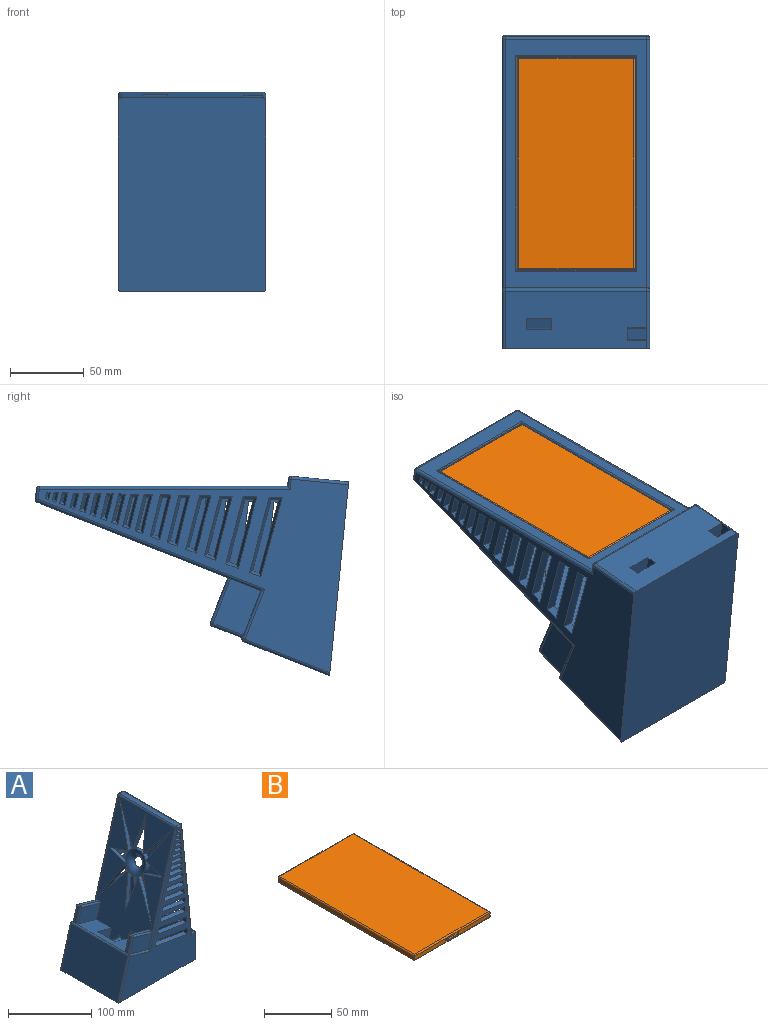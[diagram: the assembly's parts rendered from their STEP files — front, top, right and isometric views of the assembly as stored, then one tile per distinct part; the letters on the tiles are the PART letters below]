
ASSEMBLY  parts=2 mates=1
PART A: 294 faces, bbox 131.9x100x210.6 mm
  f0: plane 201.07x93mm, normal (0.96,0,-0.27), area 15915.5mm2, adj f3,f4,f9,f10,f11,f26,f27,f28
  f1: plane 200.88x96mm, normal (-0.96,0,0.27), area 12476.6mm2, adj f11,f18,f24,f25,f27,f28,f30,f31
  f2: plane 208x127.8mm, normal (0,1,0), area 9393.5mm2, adj f19,f23,f73,f78,f84,f86,f89,f94
  f3: plane 201.07x77.33mm, normal (0,-1,0), area 6368.6mm2, adj f0,f4,f26,f224,f225,f226,f227,f228
  f4: plane 201.07x93mm, normal (-1,0,-0.1), area 7026.5mm2, adj f0,f3,f6,f7,f26,f55,f136,f137
  f5: plane 96x38.96mm, normal (1,0,0), area 3497.2mm2, adj f19,f90,f92,f94,f152,f153,f154,f155
  f6: plane 80x4.04mm, normal (0.1,0,-1), area 291.7mm2, adj f4,f136,f137,f141,f142,f143,f149,f150
  f7: plane 80x4.04mm, normal (-0.1,0,1), area 292mm2, adj f4,f136,f137,f138,f139,f140,f148,f151
  f8: plane 167.24x96mm, normal (1,0,0.1), area 4160.7mm2, adj f21,f71,f73,f74,f144,f147,f292,f293
  f9: plane 6.2x1.71mm, normal (0.02,0,-1), area 5.3mm2, adj f0,f11,f134
  f10: plane 6.2x1.71mm, normal (0.02,0,-1), area 5.3mm2, adj f0,f95,f135
  f11: plane 24.74x13.23mm, normal (0,-1,0), area 152mm2, adj f0,f1,f9,f97
  f12: plane 5x1.82mm, normal (0.42,-0.91,0), area 5mm2, adj f17,f124,f131,f132,f133
  f13: plane 5x1.98mm, normal (0.99,-0.13,0), area 5mm2, adj f17,f122,f128,f129,f130
  f14: plane 5x1.98mm, normal (-0.99,0.13,0), area 5mm2, adj f17,f122,f128,f129,f130
  f15: plane 5x1.43mm, normal (-0.71,-0.7,0), area 5mm2, adj f17,f121,f125,f126,f127
  f16: plane 5x1.43mm, normal (0.71,0.7,0), area 5mm2, adj f17,f121,f125,f126,f127
  f17: plane 100x32.21mm, normal (0,0,1), area 2726.6mm2, adj f12,f13,f14,f15,f16,f27,f28,f59
  f18: plane 96x33.08mm, normal (0.27,0,0.96), area 2022.9mm2, adj f1,f24,f25,f56,f82,f86,f87,f101
  f19: plane 131.88x100mm, normal (0,0,-1), area 13184.7mm2, adj f2,f5,f20,f54,f83,f89,f90,f94
  f20: plane 208x127.8mm, normal (0,-1,0), area 9393.5mm2, adj f19,f22,f71,f75,f80,f82,f83,f90
  f21: plane 96x5mm, normal (0,0,1), area 479.5mm2, adj f8,f22,f23,f92
  f22: cylinder r=2mm len=6.81mm, axis (-1,0,0), area 17.8mm2, adj f20,f21,f71,f91
  f23: cylinder r=2mm len=6.81mm, axis (1,0,0), area 17.8mm2, adj f2,f21,f73,f93
  f24: plane 51.2x36.71mm, normal (0,-1,0), area 1128.6mm2, adj f1,f18,f56,f57,f68,f69,f70
  f25: plane 51.2x36.71mm, normal (0,1,0), area 1128.6mm2, adj f1,f18,f56,f57,f65,f66,f67
  f26: plane 93x77.33mm, normal (0,0,1), area 4899.7mm2, adj f0,f3,f4,f27,f28,f55,f60,f61
  f27: plane 30.1x8.4mm, normal (0,1,0), area 170.7mm2, adj f0,f1,f17,f26,f57,f58,f59,f60
  f28: plane 30.1x8.4mm, normal (0,-1,0), area 170.7mm2, adj f0,f1,f17,f26,f57,f58,f59,f63
  f29: cylinder r=17.15mm len=7.66mm, axis (-0.96,0,0.27), area 52.7mm2, adj f0,f30,f31,f98
  f30: plane 49.59x36.3mm, normal (-0.16,0.81,-0.57), area 365.4mm2, adj f0,f1,f29,f31,f98
  f31: plane 55.63x30.11mm, normal (0.13,-0.88,0.45), area 377.4mm2, adj f0,f1,f29,f30,f98
  f32: cylinder r=17.15mm len=17.03mm, axis (-0.96,0,0.27), area 105.4mm2, adj f0,f33,f34,f98
  f33: plane 49.43x19.37mm, normal (0.05,-0.99,0.16), area 298.6mm2, adj f0,f1,f32,f34,f98
  f34: plane 49.56x19.41mm, normal (0.05,0.99,0.16), area 299.6mm2, adj f0,f1,f32,f33,f98
  f35: cylinder r=17.15mm len=7.57mm, axis (-0.96,0,0.27), area 52.7mm2, adj f0,f36,f37,f98
  f36: plane 55.41x30.24mm, normal (-0.13,-0.88,-0.46), area 376.5mm2, adj f0,f1,f35,f37,f98
  f37: plane 49.46x36.53mm, normal (0.16,0.81,0.57), area 365.5mm2, adj f0,f1,f35,f36,f98
  f38: cylinder r=17.15mm len=17.98mm, axis (-0.96,0,0.27), area 105.2mm2, adj f0,f39,f40,f98
  f39: plane 30.05x9.7mm, normal (-0.26,-0.27,-0.93), area 184.7mm2, adj f0,f1,f38,f40,f98
  f40: plane 30.18x9.92mm, normal (0.26,-0.27,0.92), area 185.8mm2, adj f0,f1,f38,f39,f98
  f41: cylinder r=17.15mm len=17.03mm, axis (-0.96,0,0.27), area 105.4mm2, adj f0,f42,f43,f98
  f42: plane 49.44x19.36mm, normal (-0.05,0.99,-0.16), area 298.6mm2, adj f0,f1,f41,f43,f98
  f43: plane 49.56x19.4mm, normal (-0.05,-0.99,-0.16), area 299.6mm2, adj f0,f1,f41,f42,f98
  f44: cylinder r=17.15mm len=7.57mm, axis (-0.96,0,0.27), area 52.7mm2, adj f0,f45,f46,f98
  f45: plane 55.42x30.24mm, normal (0.13,0.88,0.46), area 376.5mm2, adj f0,f1,f44,f46,f98
  f46: plane 49.47x36.53mm, normal (-0.16,-0.81,-0.57), area 365.5mm2, adj f0,f1,f44,f45,f98
  f47: cylinder r=17.15mm len=7.66mm, axis (-0.96,0,0.27), area 52.7mm2, adj f0,f48,f49,f98
  f48: plane 49.59x36.3mm, normal (0.16,-0.81,0.57), area 365.4mm2, adj f0,f1,f47,f49,f98
  f49: plane 55.63x30.11mm, normal (-0.13,0.88,-0.45), area 377.4mm2, adj f0,f1,f47,f48,f98
  f50: cylinder r=17.15mm len=17.98mm, axis (-0.96,0,0.27), area 105.2mm2, adj f0,f51,f52,f98
  f51: plane 30.05x9.62mm, normal (0.27,0.27,0.93), area 184.5mm2, adj f0,f1,f50,f52,f98
  f52: plane 30.18x10mm, normal (-0.26,0.28,-0.92), area 185.9mm2, adj f0,f1,f50,f51,f98
  f53: plane 96x6.98mm, normal (0,0,1), area 669.7mm2, adj f74,f75,f78,f79
  f54: plane 96x60.08mm, normal (-0.96,0,0.27), area 5998.6mm2, adj f19,f83,f87,f89
  f55: plane 201.07x77.33mm, normal (0,1,0), area 6683.8mm2, adj f0,f4,f26,f160,f161,f162,f163,f164
  f56: plane 44.32x30mm, normal (0.96,0,-0.27), area 1383mm2, adj f18,f24,f25,f57
  f57: plane 30x24.04mm, normal (0.27,0,0.96), area 416.4mm2, adj f1,f24,f25,f27,f28,f56,f58
  f58: plane 16x2.01mm, normal (0,0,-1), area 32.2mm2, adj f27,f28,f57,f59
  f59: plane 16x8.4mm, normal (1,0,0), area 134.4mm2, adj f17,f27,f28,f58
  f60: plane 7.85x0.39mm, normal (1,0,0), area 3.1mm2, adj f17,f26,f27,f61
  f61: plane 69.9x0.39mm, normal (0,1,0), area 27.4mm2, adj f17,f26,f60,f64
  f62: plane 69.9x0.39mm, normal (0,-1,0), area 27.4mm2, adj f17,f26,f63,f64
  f63: plane 8.36x0.39mm, normal (1,0,0), area 3.3mm2, adj f17,f26,f28,f62
  f64: plane 32.21x0.39mm, normal (-1,0,0), area 12.6mm2, adj f17,f26,f61,f62
  f65: cylinder r=0.5mm len=23.25mm, axis (-0.96,0,0.27), area 37.5mm2, adj f25,f66,f67
  f66: plane 0.96x0.5mm, normal (-0.96,0,0.27), area 0.4mm2, adj f25,f65
  f67: plane 0.96x0.5mm, normal (0.96,0,-0.27), area 0.4mm2, adj f25,f65
  f68: cylinder r=0.5mm len=23.25mm, axis (-0.96,0,0.27), area 37.5mm2, adj f24,f69,f70
  f69: plane 0.96x0.5mm, normal (-0.96,0,0.27), area 0.4mm2, adj f24,f68
  f70: plane 0.96x0.5mm, normal (0.96,0,-0.27), area 0.4mm2, adj f24,f68
  f71: cylinder r=2mm len=169.24mm, axis (-0.1,0,1), area 530mm2, adj f8,f20,f22,f72
  f72: sphere r=2mm, area 5.9mm2, adj f71,f74,f75
  f73: cylinder r=2mm len=169.24mm, axis (0.1,0,-1), area 530mm2, adj f2,f8,f23,f76
  f74: cylinder r=2mm len=96mm, axis (0,-1,0), area 282.7mm2, adj f8,f53,f72,f76
  f75: cylinder r=2mm len=6.98mm, axis (1,0,0), area 21.9mm2, adj f20,f53,f72,f77
  f76: sphere r=2mm, area 5.9mm2, adj f73,f74,f78
  f77: sphere r=2mm, area 5.2mm2, adj f75,f79,f80
  f78: cylinder r=2mm len=6.98mm, axis (-1,0,0), area 21.9mm2, adj f2,f53,f76,f81
  f79: cylinder r=2mm len=96mm, axis (0,-1,0), area 248.1mm2, adj f1,f53,f77,f81
  f80: cylinder r=2mm len=159.03mm, axis (-0.27,0,-0.96), area 513.8mm2, adj f1,f20,f77,f82,f103
  f81: sphere r=2mm, area 5.2mm2, adj f78,f79,f84
  f82: cylinder r=2mm len=35.55mm, axis (-0.96,0,0.27), area 110.4mm2, adj f18,f20,f80,f85,f103
  f83: cylinder r=2mm len=60.63mm, axis (-0.27,0,-0.96), area 195.7mm2, adj f19,f20,f54,f85
  f84: cylinder r=2mm len=159.03mm, axis (0.27,0,0.96), area 513.8mm2, adj f1,f2,f81,f86,f100
  f85: sphere r=2mm, area 6.3mm2, adj f82,f83,f87
  f86: cylinder r=2mm len=35.55mm, axis (0.96,0,-0.27), area 110.4mm2, adj f2,f18,f84,f88,f100
  f87: cylinder r=2mm len=96mm, axis (0,-1,0), area 301.6mm2, adj f18,f54,f85,f88
  f88: sphere r=2mm, area 6.3mm2, adj f86,f87,f89
  f89: cylinder r=2mm len=60.63mm, axis (0.27,0,0.96), area 195.7mm2, adj f2,f19,f54,f88
  f90: cylinder r=2mm len=38.96mm, axis (0,0,1), area 122.4mm2, adj f5,f19,f20,f91
  f91: sphere r=2mm, area 6.3mm2, adj f22,f90,f92
  f92: cylinder r=2mm len=96mm, axis (0,1,0), area 301.6mm2, adj f5,f21,f91,f93
  f93: sphere r=2mm, area 6.3mm2, adj f23,f92,f94
  f94: cylinder r=2mm len=38.96mm, axis (0,0,1), area 122.4mm2, adj f2,f5,f19,f93
  f95: plane 24.74x13.23mm, normal (0,1,0), area 152mm2, adj f0,f1,f10,f96
  f96: plane 6.16x4.71mm, normal (0,0,1), area 29mm2, adj f0,f1,f27,f95
  f97: plane 6.16x4.23mm, normal (0,0,1), area 26mm2, adj f0,f1,f11,f28
  f98: torus R=17.68mm, axis (0.96,0,-0.27), area 898.6mm2, adj f0,f1,f29,f30,f31,f32,f33,f34
  f99: plane 31.15x8.91mm, normal (0.27,0,0.96), area 121.5mm2, adj f1,f115,f118,f120
  f100: plane 37.2x30.06mm, normal (0,1,0), area 712.8mm2, adj f84,f86,f114,f115
  f101: plane 37.2x30.06mm, normal (0,-1,0), area 712.8mm2, adj f1,f18,f117,f120
  f102: plane 21.15x6.05mm, normal (-0.96,0,0.27), area 82.5mm2, adj f18,f114,f117,f118
  f103: plane 37.2x30.06mm, normal (0,-1,0), area 712.8mm2, adj f80,f82,f110,f113
  f104: plane 31.15x8.91mm, normal (0.27,0,0.96), area 121.5mm2, adj f1,f108,f111,f113
  f105: plane 37.2x30.06mm, normal (0,1,0), area 712.8mm2, adj f1,f18,f107,f108
  f106: plane 21.15x6.05mm, normal (-0.96,0,0.27), area 82.5mm2, adj f18,f107,f110,f111
  f107: cylinder r=2mm len=21.7mm, axis (0.27,0,0.96), area 69.1mm2, adj f18,f105,f106,f109
  f108: cylinder r=2mm len=31.7mm, axis (0.96,0,-0.27), area 101.8mm2, adj f1,f104,f105,f109
  f109: sphere r=2mm, area 6.3mm2, adj f107,f108,f111
  f110: cylinder r=2mm len=21.7mm, axis (-0.27,0,-0.96), area 69.1mm2, adj f18,f103,f106,f112
  f111: cylinder r=2mm len=3.75mm, axis (0,-1,0), area 11.8mm2, adj f104,f106,f109,f112
  f112: sphere r=2mm, area 6.3mm2, adj f110,f111,f113
  f113: cylinder r=2mm len=31.7mm, axis (0.96,0,-0.27), area 101.8mm2, adj f1,f103,f104,f112
  f114: cylinder r=2mm len=21.7mm, axis (0.27,0,0.96), area 69.1mm2, adj f18,f100,f102,f116
  f115: cylinder r=2mm len=31.7mm, axis (-0.96,0,0.27), area 101.8mm2, adj f1,f99,f100,f116
  f116: sphere r=2mm, area 6.3mm2, adj f114,f115,f118
  f117: cylinder r=2mm len=21.7mm, axis (-0.27,0,-0.96), area 69.1mm2, adj f18,f101,f102,f119
  f118: cylinder r=2mm len=3.75mm, axis (0,-1,0), area 11.8mm2, adj f99,f102,f116,f119
  f119: sphere r=2mm, area 6.3mm2, adj f117,f118,f120
  f120: cylinder r=2mm len=31.7mm, axis (0.96,0,-0.27), area 101.8mm2, adj f1,f99,f101,f119
  f121: plane 5x1.62mm, normal (0.7,-0.71,0), area 11.3mm2, adj f15,f16,f17,f125
  f122: plane 5x2.24mm, normal (0.13,0.99,0), area 11.3mm2, adj f13,f14,f17,f130
  f123: plane 5x1.82mm, normal (-0.42,0.91,0), area 5mm2, adj f17,f124,f131,f132,f133
  f124: plane 5x2.05mm, normal (-0.91,-0.42,0), area 11.3mm2, adj f12,f17,f123,f133
  f125: plane 3.02x3.01mm, normal (-0.49,0.51,0.71), area 6.4mm2, adj f15,f16,f121,f126
  f126: plane 2.32x2.3mm, normal (0,0,-1), area 2.3mm2, adj f15,f16,f125,f127
  f127: plane 3x1.62mm, normal (-0.7,0.71,0), area 6.8mm2, adj f15,f16,f17,f126
  f128: plane 2.38x1.3mm, normal (0,0,-1), area 2.3mm2, adj f13,f14,f129,f130
  f129: plane 3x2.24mm, normal (-0.13,-0.99,0), area 6.8mm2, adj f13,f14,f17,f128
  f130: plane 2.51x2.29mm, normal (-0.1,-0.7,0.71), area 6.4mm2, adj f13,f14,f122,f128
  f131: plane 2.47x1.86mm, normal (0,0,-1), area 2.3mm2, adj f12,f123,f132,f133
  f132: plane 3x2.05mm, normal (0.91,0.42,0), area 6.8mm2, adj f12,f17,f123,f131
  f133: plane 2.89x2.76mm, normal (0.64,0.3,0.71), area 6.4mm2, adj f12,f123,f124,f131
  f134: plane 12.78x12.47mm, normal (-0.19,-0.73,-0.66), area 100.5mm2, adj f0,f1,f9,f135
  f135: plane 12.78x12.47mm, normal (-0.19,0.73,-0.66), area 100.5mm2, adj f0,f1,f10,f134
  f136: plane 143.83x18.59mm, normal (0,1,0), area 643.8mm2, adj f4,f6,f7,f148,f149,f292
  f137: plane 143.83x18.59mm, normal (0,-1,0), area 643.8mm2, adj f4,f6,f7,f148,f149,f293
  f138: cylinder r=0.5mm len=20mm, axis (0,-1,0), area 25.6mm2, adj f7,f139,f140,f145
  f139: plane 1.62x0.6mm, normal (0,-1,0), area 0.4mm2, adj f7,f138,f145,f151
  f140: plane 1.62x0.6mm, normal (0,1,0), area 0.4mm2, adj f7,f138,f145,f151
  f141: cylinder r=0.5mm len=20mm, axis (0,-1,0), area 26.8mm2, adj f6,f142,f143,f146
  f142: plane 1.64x0.56mm, normal (0,-1,0), area 0.5mm2, adj f6,f141,f146,f150
  f143: plane 1.64x0.56mm, normal (0,1,0), area 0.5mm2, adj f6,f141,f146,f150
  f144: plane 82x0.77mm, normal (0.63,0,0.77), area 80.6mm2, adj f8,f148,f292,f293
  f145: plane 20x0.2mm, normal (-0.57,0,0.82), area 4.9mm2, adj f138,f139,f140,f151
  f146: plane 20x0.2mm, normal (-0.42,0,-0.91), area 4.4mm2, adj f141,f142,f143,f150
  f147: plane 82x0.77mm, normal (0.77,0,-0.63), area 80.6mm2, adj f8,f149,f292,f293
  f148: cylinder r=1mm len=80.09mm, axis (0,1,0), area 62.8mm2, adj f7,f136,f137,f144,f292,f293
  f149: cylinder r=1mm len=80.09mm, axis (0,-1,0), area 62.8mm2, adj f6,f136,f137,f147,f292,f293
  f150: cylinder r=1mm len=20mm, axis (0,-1,0), area 10.7mm2, adj f6,f142,f143,f146
  f151: cylinder r=1mm len=20mm, axis (0,-1,0), area 10.2mm2, adj f7,f139,f140,f145
  f152: plane 12.84x9.86mm, normal (0,0,-1), area 126.6mm2, adj f4,f5,f153,f155
  f153: plane 9.86x8.83mm, normal (0,1,0), area 83.2mm2, adj f4,f5,f152,f154
  f154: plane 12.84x8.99mm, normal (0,0,1), area 115.4mm2, adj f4,f5,f153,f155
  f155: plane 9.86x8.83mm, normal (0,-1,0), area 83.2mm2, adj f4,f5,f152,f154
  f156: plane 17.15x10.48mm, normal (0,0,-1), area 179.7mm2, adj f4,f5,f157,f159
  f157: plane 10.48x7.55mm, normal (0,1,0), area 76.3mm2, adj f4,f5,f156,f158
  f158: plane 17.15x9.73mm, normal (0,0,1), area 166.9mm2, adj f4,f5,f157,f159
  f159: plane 10.48x7.55mm, normal (0,-1,0), area 76.3mm2, adj f4,f5,f156,f158
  f160: plane 5x3.7mm, normal (0.91,-0.34,-0.23), area 10.6mm2, adj f20,f55,f161,f163
  f161: plane 8.6x5mm, normal (0.13,-0.34,0.93), area 34.8mm2, adj f20,f55,f160,f162
  f162: plane 5x3.88mm, normal (-0.94,-0.34,-0.07), area 10.8mm2, adj f20,f55,f161,f163
  f163: plane 7.35x5mm, normal (-0.13,-0.34,-0.93), area 31.3mm2, adj f20,f55,f160,f162
  f164: plane 5x4.04mm, normal (0.91,-0.34,-0.23), area 12.5mm2, adj f20,f55,f165,f167
  f165: plane 13.4x5mm, normal (0.13,-0.34,0.93), area 60.6mm2, adj f20,f55,f164,f166
  f166: plane 5x4.24mm, normal (-0.94,-0.34,-0.07), area 12.7mm2, adj f20,f55,f165,f167
  f167: plane 12.04x5mm, normal (-0.13,-0.34,-0.93), area 56.5mm2, adj f20,f55,f164,f166
  f168: plane 5x3.9mm, normal (0.91,-0.34,-0.23), area 11.7mm2, adj f20,f55,f169,f171
  f169: plane 15.79x5mm, normal (0.13,-0.34,0.93), area 73.5mm2, adj f20,f55,f168,f170
  f170: plane 5x4.09mm, normal (-0.94,-0.34,-0.07), area 11.9mm2, adj f20,f55,f169,f171
  f171: plane 14.48x5mm, normal (-0.13,-0.34,-0.93), area 69.6mm2, adj f20,f55,f168,f170
  f172: plane 5x4.31mm, normal (0.91,-0.34,-0.23), area 13.9mm2, adj f20,f55,f173,f175
  f173: plane 18.45x5mm, normal (0.13,-0.34,0.93), area 87.8mm2, adj f20,f55,f172,f174
  f174: plane 5x4.52mm, normal (-0.94,-0.34,-0.07), area 14.2mm2, adj f20,f55,f173,f175
  f175: plane 17x5mm, normal (-0.13,-0.34,-0.93), area 83.2mm2, adj f20,f55,f172,f174
  f176: plane 5x4.42mm, normal (0.91,-0.34,-0.23), area 14.5mm2, adj f20,f55,f177,f179
  f177: plane 21.1x5mm, normal (0.13,-0.34,0.93), area 102mm2, adj f20,f55,f176,f178
  f178: plane 5x4.64mm, normal (-0.94,-0.34,-0.07), area 14.8mm2, adj f20,f55,f177,f179
  f179: plane 19.61x5mm, normal (-0.13,-0.34,-0.93), area 97.2mm2, adj f20,f55,f176,f178
  f180: plane 5.1x5mm, normal (0.91,-0.34,-0.23), area 18.3mm2, adj f20,f55,f181,f183
  f181: plane 23.91x5mm, normal (0.13,-0.34,0.93), area 117.1mm2, adj f20,f55,f180,f182
  f182: plane 5.35x5mm, normal (-0.94,-0.34,-0.07), area 18.6mm2, adj f20,f55,f181,f183
  f183: plane 22.19x5mm, normal (-0.13,-0.34,-0.93), area 111.1mm2, adj f20,f55,f180,f182
  f184: plane 5.29x5mm, normal (0.91,-0.34,-0.23), area 19.3mm2, adj f20,f55,f185,f187
  f185: plane 26.95x5.41mm, normal (0.13,-0.34,0.93), area 133.5mm2, adj f20,f55,f184,f186
  f186: plane 5.55x5mm, normal (-0.94,-0.34,-0.07), area 19.7mm2, adj f20,f55,f185,f187
  f187: plane 25.16x5.23mm, normal (-0.13,-0.34,-0.93), area 127.1mm2, adj f20,f55,f184,f186
  f188: plane 6.86x5mm, normal (0.91,-0.34,-0.23), area 28mm2, adj f20,f55,f189,f191
  f189: plane 30.99x6mm, normal (0.13,-0.34,0.93), area 155.2mm2, adj f20,f55,f188,f190
  f190: plane 7.2x5mm, normal (-0.94,-0.34,-0.07), area 28.5mm2, adj f20,f55,f189,f191
  f191: plane 28.67x5.74mm, normal (-0.13,-0.34,-0.93), area 145.9mm2, adj f20,f55,f188,f190
  f192: plane 8.78x5mm, normal (0.91,-0.34,-0.23), area 38.5mm2, adj f20,f55,f193,f195
  f193: plane 49.52x9.16mm, normal (0.14,-0.34,0.93), area 255.2mm2, adj f20,f55,f192,f194
  f194: plane 9.24x5mm, normal (-0.94,-0.34,-0.07), area 39.4mm2, adj f20,f55,f193,f195
  f195: plane 46.55x8.78mm, normal (-0.14,-0.34,-0.93), area 242.4mm2, adj f20,f55,f192,f194
  f196: plane 7.83x5mm, normal (0.9,-0.34,-0.26), area 33.5mm2, adj f20,f55,f197,f199
  f197: plane 44.17x8.32mm, normal (0.14,-0.34,0.93), area 226.2mm2, adj f20,f55,f196,f198
  f198: plane 8.27x5mm, normal (-0.94,-0.34,-0.07), area 34.2mm2, adj f20,f55,f197,f199
  f199: plane 41.31x7.97mm, normal (-0.14,-0.34,-0.93), area 214.3mm2, adj f20,f55,f196,f198
  f200: plane 7.28x5mm, normal (0.91,-0.34,-0.23), area 30.3mm2, adj f20,f55,f201,f203
  f201: plane 39.57x7.62mm, normal (0.14,-0.34,0.93), area 201.6mm2, adj f20,f55,f200,f202
  f202: plane 7.66x5mm, normal (-0.94,-0.34,-0.07), area 30.9mm2, adj f20,f55,f201,f203
  f203: plane 37.11x7.32mm, normal (-0.14,-0.34,-0.93), area 191.6mm2, adj f20,f55,f200,f202
  f204: plane 6.91x5mm, normal (0.91,-0.34,-0.23), area 28.2mm2, adj f20,f55,f205,f207
  f205: plane 35.03x6.58mm, normal (0.13,-0.34,0.93), area 176.9mm2, adj f20,f55,f204,f206
  f206: plane 7.25x5mm, normal (-0.94,-0.34,-0.07), area 28.8mm2, adj f20,f55,f205,f207
  f207: plane 32.69x6.32mm, normal (-0.13,-0.34,-0.93), area 167.5mm2, adj f20,f55,f204,f206
  f208: plane 7.77x5mm, normal (0.91,-0.34,-0.23), area 33mm2, adj f20,f55,f209,f211
  f209: plane 54.87x10.65mm, normal (0.16,-0.34,0.93), area 284.6mm2, adj f20,f55,f208,f210
  f210: plane 8.87x5mm, normal (-0.94,-0.34,-0.07), area 37.3mm2, adj f20,f55,f209,f211
  f211: plane 52.19x9.66mm, normal (-0.14,-0.34,-0.93), area 272.8mm2, adj f20,f55,f208,f210
  f212: plane 3.32x2.36mm, normal (0.91,-0.34,-0.23), area 4.3mm2, adj f20,f213,f215
  f213: plane 4.77x3.32mm, normal (0.13,-0.34,0.93), area 12mm2, adj f20,f212,f214,f215
  f214: plane 3.32x2.47mm, normal (-0.94,-0.34,-0.07), area 4.4mm2, adj f20,f213,f215
  f215: plane 3.98x3.32mm, normal (-0.13,-0.34,-0.93), area 10.6mm2, adj f20,f212,f213,f214
  f216: plane 3.92x2.78mm, normal (0.91,-0.34,-0.23), area 6mm2, adj f20,f217,f219
  f217: plane 6.49x3.92mm, normal (0.13,-0.34,0.93), area 20.3mm2, adj f20,f216,f218,f219
  f218: plane 3.92x2.92mm, normal (-0.94,-0.34,-0.07), area 6.1mm2, adj f20,f217,f219
  f219: plane 5.55x3.92mm, normal (-0.13,-0.34,-0.93), area 18.4mm2, adj f20,f216,f217,f218
  f220: plane 4.93x3.5mm, normal (0.91,-0.34,-0.23), area 9.5mm2, adj f20,f221,f223
  f221: plane 10.97x4.93mm, normal (0.13,-0.34,0.93), area 47mm2, adj f20,f220,f222,f223
  f222: plane 4.93x3.67mm, normal (-0.94,-0.34,-0.07), area 9.7mm2, adj f20,f221,f223
  f223: plane 9.78x4.93mm, normal (-0.13,-0.34,-0.93), area 43.9mm2, adj f20,f220,f221,f222
  f224: plane 2.86x2mm, normal (-0.82,0.57,-0.06), area 3.6mm2, adj f2,f3,f225,f227
  f225: plane 6.56x2mm, normal (0.03,0.57,0.82), area 12mm2, adj f2,f3,f224,f226
  f226: plane 2.83x2mm, normal (0.79,0.57,-0.2), area 3.6mm2, adj f2,f3,f225,f227
  f227: plane 5.61x2mm, normal (-0.03,0.57,-0.82), area 10.8mm2, adj f2,f3,f224,f226
  f228: plane 3.81x2mm, normal (-0.82,0.57,-0.06), area 5.9mm2, adj f2,f3,f229,f231
  f229: plane 8.69x2mm, normal (0.03,0.57,0.82), area 17.2mm2, adj f2,f3,f228,f230
  f230: plane 3.77x2.05mm, normal (0.79,0.57,-0.2), area 6mm2, adj f2,f3,f229,f231
  f231: plane 7.42x2mm, normal (-0.03,0.57,-0.82), area 15.2mm2, adj f2,f3,f228,f230
  f232: plane 3.6x2mm, normal (-0.82,0.57,-0.06), area 5.4mm2, adj f2,f3,f233,f235
  f233: plane 11.08x2mm, normal (0.03,0.57,0.82), area 23mm2, adj f2,f3,f232,f234
  f234: plane 3.57x2mm, normal (0.79,0.57,-0.2), area 5.5mm2, adj f2,f3,f233,f235
  f235: plane 9.88x2mm, normal (-0.03,0.57,-0.82), area 21.2mm2, adj f2,f3,f232,f234
  f236: plane 4.16x2mm, normal (-0.82,0.57,-0.06), area 6.7mm2, adj f2,f3,f237,f239
  f237: plane 13.54x2mm, normal (0.03,0.57,0.82), area 29mm2, adj f2,f3,f236,f238
  f238: plane 4.12x2.14mm, normal (0.79,0.57,-0.2), area 6.9mm2, adj f2,f3,f237,f239
  f239: plane 12.16x2mm, normal (-0.03,0.57,-0.82), area 26.8mm2, adj f2,f3,f236,f238
  f240: plane 4.01x2mm, normal (-0.82,0.57,-0.06), area 6.4mm2, adj f2,f3,f241,f243
  f241: plane 15.95x2mm, normal (0.03,0.57,0.82), area 34.9mm2, adj f2,f3,f240,f242
  f242: plane 3.97x2.1mm, normal (0.79,0.57,-0.2), area 6.5mm2, adj f2,f3,f241,f243
  f243: plane 14.62x2mm, normal (-0.03,0.57,-0.82), area 32.8mm2, adj f2,f3,f240,f242
  f244: plane 4.44x2mm, normal (-0.82,0.57,-0.06), area 7.4mm2, adj f2,f3,f245,f247
  f245: plane 18.64x2mm, normal (0.03,0.57,0.82), area 41.5mm2, adj f2,f3,f244,f246
  f246: plane 4.39x2.21mm, normal (0.79,0.57,-0.2), area 7.6mm2, adj f2,f3,f245,f247
  f247: plane 17.16x2mm, normal (-0.03,0.57,-0.82), area 39mm2, adj f2,f3,f244,f246
  f248: plane 4.55x2mm, normal (-0.82,0.57,-0.06), area 7.7mm2, adj f2,f3,f249,f251
  f249: plane 21.31x2mm, normal (0.03,0.57,0.82), area 48mm2, adj f2,f3,f248,f250
  f250: plane 4.5x2.24mm, normal (0.79,0.57,-0.2), area 7.8mm2, adj f2,f3,f249,f251
  f251: plane 19.8x2mm, normal (-0.03,0.57,-0.82), area 45.5mm2, adj f2,f3,f248,f250
  f252: plane 5.25x2mm, normal (-0.82,0.57,-0.06), area 9.4mm2, adj f2,f3,f253,f255
  f253: plane 24.15x2.09mm, normal (0.03,0.57,0.82), area 54.9mm2, adj f2,f3,f252,f254
  f254: plane 5.19x2.42mm, normal (0.79,0.57,-0.2), area 9.6mm2, adj f2,f3,f253,f255
  f255: plane 22.41x2.05mm, normal (-0.03,0.57,-0.82), area 51.8mm2, adj f2,f3,f252,f254
  f256: plane 5.45x2mm, normal (-0.82,0.57,-0.06), area 9.9mm2, adj f2,f3,f257,f259
  f257: plane 27.22x2.19mm, normal (0.03,0.57,0.82), area 62.4mm2, adj f2,f3,f256,f258
  f258: plane 5.39x2.47mm, normal (0.79,0.57,-0.2), area 10.1mm2, adj f2,f3,f257,f259
  f259: plane 25.41x2.14mm, normal (-0.03,0.57,-0.82), area 59.2mm2, adj f2,f3,f256,f258
  f260: plane 7.07x2mm, normal (-0.82,0.57,-0.06), area 13.9mm2, adj f2,f3,f261,f263
  f261: plane 31.3x2.31mm, normal (0.03,0.57,0.82), area 72.4mm2, adj f2,f3,f260,f262
  f262: plane 6.99x2.88mm, normal (0.79,0.57,-0.2), area 14.1mm2, adj f2,f3,f261,f263
  f263: plane 28.96x2.25mm, normal (-0.03,0.57,-0.82), area 67.8mm2, adj f2,f3,f260,f262
  f264: plane 7.11x2mm, normal (-0.82,0.57,-0.06), area 14mm2, adj f2,f3,f265,f267
  f265: plane 35.37x2.44mm, normal (0.03,0.57,0.82), area 82.4mm2, adj f2,f3,f264,f266
  f266: plane 7.04x2.89mm, normal (0.79,0.57,-0.2), area 14.2mm2, adj f2,f3,f265,f267
  f267: plane 33.02x2.38mm, normal (-0.03,0.57,-0.82), area 77.7mm2, adj f2,f3,f264,f266
  f268: plane 7.49x2mm, normal (-0.82,0.57,-0.06), area 14.9mm2, adj f2,f3,f269,f271
  f269: plane 40.03x2.2mm, normal (0.02,0.57,0.82), area 93.7mm2, adj f2,f3,f268,f270
  f270: plane 7.44x3mm, normal (0.79,0.57,-0.2), area 15.2mm2, adj f2,f3,f269,f271
  f271: plane 37.54x2.16mm, normal (-0.02,0.57,-0.82), area 88.8mm2, adj f2,f3,f268,f270
  f272: plane 8.09x2.09mm, normal (-0.81,0.57,-0.08), area 16.4mm2, adj f2,f3,f273,f275
  f273: plane 44.68x2.3mm, normal (0.02,0.57,0.82), area 105mm2, adj f2,f3,f272,f274
  f274: plane 8.03x3.15mm, normal (0.79,0.57,-0.2), area 16.7mm2, adj f2,f3,f273,f275
  f275: plane 41.79x2.25mm, normal (-0.02,0.57,-0.82), area 99.2mm2, adj f2,f3,f272,f274
  f276: plane 9.04x2mm, normal (-0.82,0.57,-0.06), area 18.7mm2, adj f2,f3,f277,f279
  f277: plane 50.1x2.41mm, normal (0.02,0.57,0.82), area 118.3mm2, adj f2,f3,f276,f278
  f278: plane 8.97x3.39mm, normal (0.79,0.57,-0.2), area 19.1mm2, adj f2,f3,f277,f279
  f279: plane 47.1x2.36mm, normal (-0.02,0.57,-0.82), area 112.1mm2, adj f2,f3,f276,f278
  f280: plane 52.8x2.48mm, normal (-0.02,0.57,-0.82), area 126mm2, adj f2,f3,f282,f283
  f281: plane 55.63x2mm, normal (0.01,0.57,0.82), area 131.8mm2, adj f2,f3,f282,f283
  f282: plane 8x2mm, normal (-0.82,0.57,-0.06), area 16.2mm2, adj f2,f3,f280,f281
  f283: plane 8.62x3.3mm, normal (0.79,0.57,-0.2), area 18.2mm2, adj f2,f3,f280,f281
  f284: plane 2.42x1.73mm, normal (-0.82,0.57,-0.06), area 2.6mm2, adj f2,f285,f287
  f285: plane 4.82x1.73mm, normal (0.03,0.57,0.82), area 7.1mm2, adj f2,f284,f286,f287
  f286: plane 2.4x1.73mm, normal (0.79,0.57,-0.2), area 2.6mm2, adj f2,f285,f287
  f287: plane 4.02x1.73mm, normal (-0.03,0.57,-0.82), area 6.3mm2, adj f2,f284,f285,f286
  f288: plane 11.38x8.01mm, normal (0.48,0.87,-0.14), area 57.6mm2, adj f0,f1,f289,f291
  f289: plane 16.84x6.63mm, normal (0.24,0,-0.97), area 91.8mm2, adj f0,f1,f288,f290
  f290: plane 11.38x8.01mm, normal (0.48,-0.87,-0.14), area 57.6mm2, adj f0,f1,f289,f291
  f291: plane 16.84x4.92mm, normal (0.72,0,0.7), area 91.8mm2, adj f0,f1,f288,f290
  f292: cylinder r=1mm len=145.39mm, axis (0.1,0,-1), area 228.2mm2, adj f8,f136,f144,f147,f148,f149
  f293: cylinder r=1mm len=145.39mm, axis (-0.1,0,1), area 228.2mm2, adj f8,f137,f144,f147,f148,f149
PART B: 58 faces, bbox 79.8x144.8x5.5 mm
  f0: plane 32.3x3.47mm, normal (0,1,0), area 112.1mm2, adj f25,f40,f46,f51
  f1: plane 10x1.24mm, normal (0,1,0), area 12.3mm2, adj f35,f36,f37,f46
  f2: plane 32.5x3.47mm, normal (0,1,0), area 112.8mm2, adj f26,f39,f46,f51
  f3: plane 32.5x3.47mm, normal (0,-1,0), area 112.8mm2, adj f14,f38,f45,f56
  f4: plane 10x1.24mm, normal (0,-1,0), area 12.3mm2, adj f32,f33,f34,f45
  f5: plane 32.3x3.47mm, normal (0,-1,0), area 112.1mm2, adj f15,f41,f45,f56
  f6: plane 10x3.47mm, normal (0,1,0), area 34.7mm2, adj f9,f11,f33,f34
  f7: plane 3.47x2.8mm, normal (0,1,0), area 9.7mm2, adj f9,f11,f13,f15
  f8: plane 20x3.47mm, normal (0,-1,0), area 69.4mm2, adj f9,f11,f12,f13
  f9: plane 20x2mm, normal (0,0,1), area 24mm2, adj f6,f7,f8,f10,f12,f13,f14,f15
  f10: plane 3.47x3.2mm, normal (0,1,0), area 11.1mm2, adj f9,f11,f12,f14
  f11: plane 20x2mm, normal (0,0,-1), area 24mm2, adj f6,f7,f8,f10,f12,f13,f14,f15
  f12: plane 3.47x1mm, normal (-1,0,0), area 3.5mm2, adj f8,f9,f10,f11
  f13: plane 3.47x1mm, normal (1,0,0), area 3.5mm2, adj f7,f8,f9,f11
  f14: plane 3.47x1mm, normal (-1,0,0), area 3.5mm2, adj f3,f9,f10,f11
  f15: plane 3.47x1mm, normal (1,0,0), area 3.5mm2, adj f5,f7,f9,f11
  f16: plane 10x1.24mm, normal (0,-1,0), area 12.4mm2, adj f32,f33,f34,f56
  f17: plane 10x3.47mm, normal (0,-1,0), area 34.7mm2, adj f20,f22,f36,f37
  f18: plane 3.47x3.2mm, normal (0,-1,0), area 11.1mm2, adj f20,f22,f23,f26
  f19: plane 3.47x2.8mm, normal (0,-1,0), area 9.7mm2, adj f20,f22,f24,f25
  f20: plane 20x2mm, normal (0,0,1), area 24mm2, adj f17,f18,f19,f21,f23,f24,f25,f26
  f21: plane 20x3.47mm, normal (0,1,0), area 69.4mm2, adj f20,f22,f23,f24
  f22: plane 20x2mm, normal (0,0,-1), area 24mm2, adj f17,f18,f19,f21,f23,f24,f25,f26
  f23: plane 3.47x1mm, normal (-1,0,0), area 3.5mm2, adj f18,f20,f21,f22
  f24: plane 3.47x1mm, normal (1,0,0), area 3.5mm2, adj f19,f20,f21,f22
  f25: plane 3.47x1mm, normal (1,0,0), area 3.5mm2, adj f0,f19,f20,f22
  f26: plane 3.47x1mm, normal (-1,0,0), area 3.5mm2, adj f2,f18,f20,f22
  f27: plane 142.8x3.47mm, normal (1,0,0), area 495.5mm2, adj f38,f39,f42,f55
  f28: plane 10x1.24mm, normal (0,1,0), area 12.3mm2, adj f35,f36,f37,f51
  f29: plane 142.8x3.47mm, normal (-1,0,0), area 495.5mm2, adj f40,f41,f49,f52
  f30: plane 141.8x77.8mm, normal (0,0,1), area 11032mm2, adj f42,f45,f46,f49
  f31: plane 141.8x77.8mm, normal (0,0,-1), area 11032mm2, adj f51,f52,f55,f56
  f32: cylinder r=0.5mm len=10mm, axis (1,0,0), area 15.7mm2, adj f4,f16,f33,f34
  f33: plane 3.47x1.5mm, normal (-1,0,0), area 3.9mm2, adj f4,f6,f9,f11,f16,f32
  f34: plane 3.47x1.5mm, normal (1,0,0), area 3.9mm2, adj f4,f6,f9,f11,f16,f32
  f35: cylinder r=0.5mm len=10mm, axis (1,0,0), area 15.7mm2, adj f1,f28,f36,f37
  f36: plane 3.47x1.5mm, normal (-1,0,0), area 3.9mm2, adj f1,f17,f20,f22,f28,f35
  f37: plane 3.47x1.5mm, normal (1,0,0), area 3.9mm2, adj f1,f17,f20,f22,f28,f35
  f38: cylinder r=0.5mm len=3.47mm, axis (0,0,1), area 2.7mm2, adj f3,f27,f43,f57
  f39: cylinder r=0.5mm len=3.47mm, axis (0,0,-1), area 2.7mm2, adj f2,f27,f44,f53
  f40: cylinder r=0.5mm len=3.47mm, axis (0,0,1), area 2.7mm2, adj f0,f29,f48,f50
  f41: cylinder r=0.5mm len=3.47mm, axis (0,0,-1), area 2.7mm2, adj f5,f29,f47,f54
  f42: cylinder r=1mm len=142.8mm, axis (0,-1,0), area 223.7mm2, adj f27,f30,f43,f44
  f43: bspline ~1.19x1mm, area 0.8mm2, adj f38,f42,f45
  f44: bspline ~1.19x1mm, area 0.8mm2, adj f39,f42,f46
  f45: cylinder r=1mm len=78.8mm, axis (-1,0,0), area 123.2mm2, adj f3,f4,f5,f11,f30,f43,f47
  f46: cylinder r=1mm len=78.8mm, axis (1,0,0), area 123.2mm2, adj f0,f1,f2,f22,f30,f44,f48
  f47: bspline ~1.19x1mm, area 0.8mm2, adj f41,f45,f49
  f48: bspline ~1.19x1mm, area 0.8mm2, adj f40,f46,f49
  f49: cylinder r=1mm len=142.8mm, axis (0,1,0), area 223.7mm2, adj f29,f30,f47,f48
  f50: bspline ~1.19x1mm, area 0.8mm2, adj f40,f51,f52
  f51: cylinder r=1mm len=78.8mm, axis (-1,0,0), area 123.2mm2, adj f0,f2,f20,f28,f31,f50,f53
  f52: cylinder r=1mm len=142.8mm, axis (0,-1,0), area 223.7mm2, adj f29,f31,f50,f54
  f53: bspline ~1.19x1mm, area 0.8mm2, adj f39,f51,f55
  f54: bspline ~1.19x1mm, area 0.8mm2, adj f41,f52,f56
  f55: cylinder r=1mm len=142.8mm, axis (0,1,0), area 223.7mm2, adj f27,f31,f53,f57
  f56: cylinder r=1mm len=78.8mm, axis (1,0,0), area 123.2mm2, adj f3,f5,f9,f16,f31,f54,f57
  f57: bspline ~1.19x1mm, area 0.8mm2, adj f38,f55,f56
PLACE A rot(axis=(-0.56,-0.56,-0.62),116.8deg) t=(117.74,-34.06,93.33)mm
PLACE B rot(axis=(1,0,0),180deg) t=(67.84,-19.01,138.57)mm
MATE fastened B.f28 <-> A.f7  axis (0,-1,0) through (67.74,-90.91,137.57)mm
